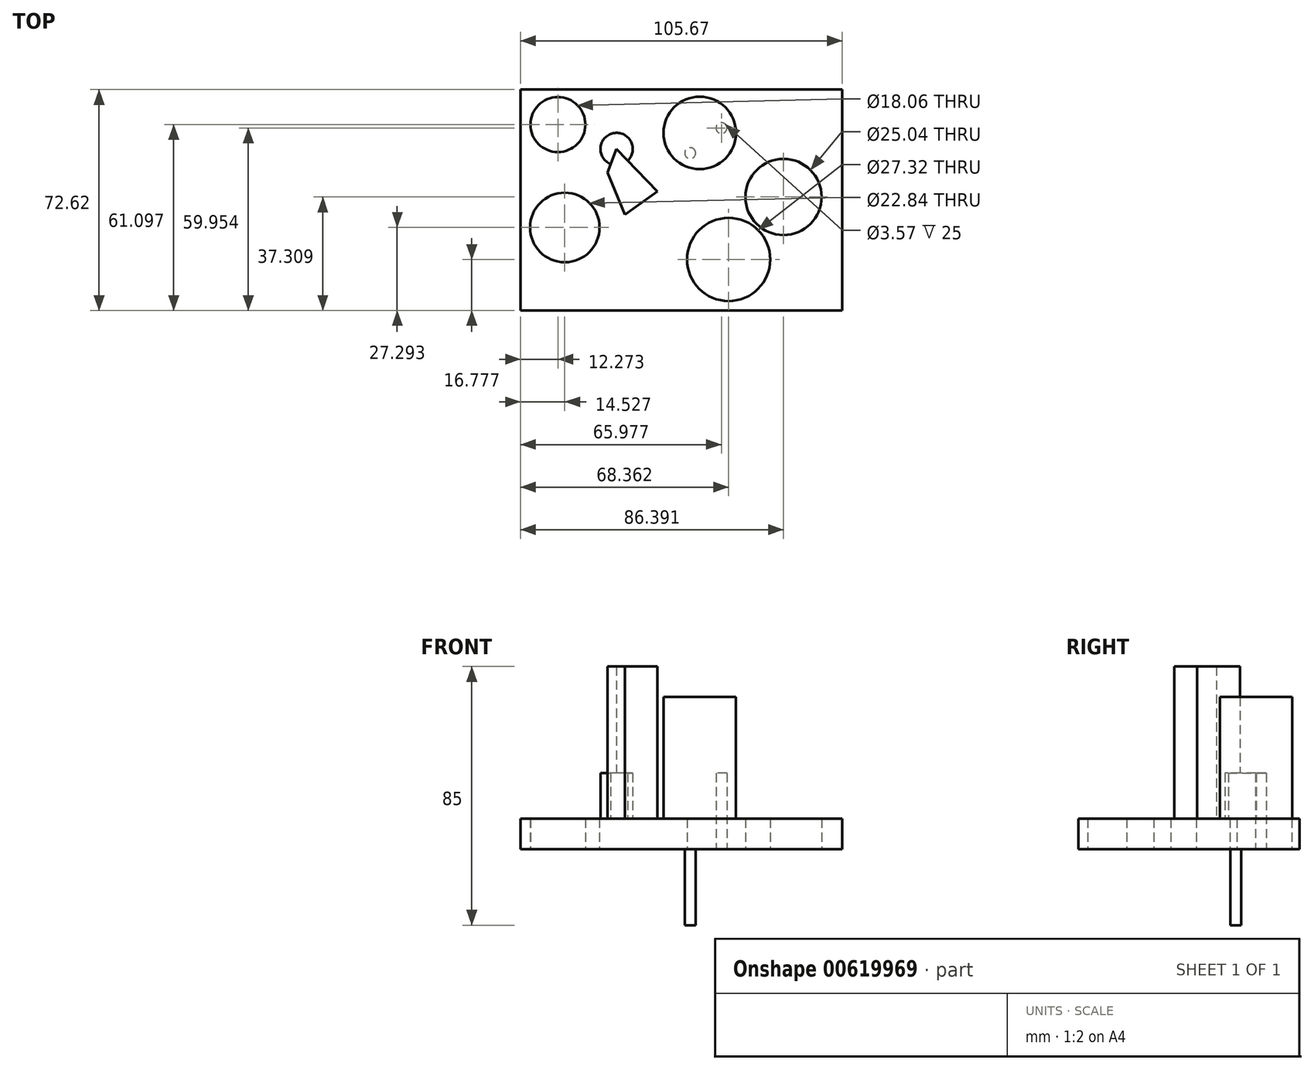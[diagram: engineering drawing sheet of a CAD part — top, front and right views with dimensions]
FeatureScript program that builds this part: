
annotation { "Feature Type Name" : "Feature", "Feature Type Description" : "" }
export const myFeature = defineFeature(function(context is Context, id is Id, definition is map)
    precondition{}
    {
        {
            var Q0;
            Q0=qCreatedBy(makeId("Top.planeOp"),FACE);
            var sketch = newSketch(context, id + "F0", { "sketchPlane" : qUnion([Q0])});
            skLineSegment(sketch, "E0.bottom", {"start": v(-44.95, 41.07) * mm, "end": v(60.72, 41.07) * mm});
            skLineSegment(sketch, "E0.top", {"start": v(-44.95, -31.55) * mm, "end": v(60.72, -31.55) * mm});
            skLineSegment(sketch, "E0.left", {"start": v(-44.95, 41.07) * mm, "end": v(-44.95, -31.55) * mm});
            skLineSegment(sketch, "E0.right", {"start": v(60.72, 41.07) * mm, "end": v(60.72, -31.55) * mm});
            skCircle(sketch, "E1", {"center": v(-32.68, 29.55) * mm, "radius": 9.03 * mm});
            skCircle(sketch, "E2", {"center": v(13.9, 26.8) * mm, "radius": 11.9 * mm});
            skCircle(sketch, "E3", {"center": v(41.44, 5.76) * mm, "radius": 12.52 * mm});
            skCircle(sketch, "E4", {"center": v(23.41, -14.77) * mm, "radius": 13.66 * mm});
            skCircle(sketch, "E5", {"center": v(-30.42, -4.26) * mm, "radius": 11.42 * mm});
            skLineSegment(sketch, "E6", {"start": v(-13.4, 21.53) * mm, "end": v(-16.4, 13.77) * mm});
            skLineSegment(sketch, "E7", {"start": v(-16.4, 13.77) * mm, "end": v(-10.72, 0) * mm});
            skLineSegment(sketch, "E8", {"start": v(-10.72, 0) * mm, "end": v(0, 7.51) * mm});
            skLineSegment(sketch, "E9", {"start": v(0, 7.51) * mm, "end": v(-13.4, 21.53) * mm});
            skArc(sketch, "E10", {"start": v(-9.73, 17.7) * mm, "mid": v(-14.43, 26.74) * mm, "end": v(-15.31, 16.58) * mm});
            skCircle(sketch, "E11", {"center": v(13.9, 26.8) * mm, "radius": 7.31 * mm, "construction": true});
            skCircle(sketch, "E12", {"center": v(6.6, 27.14) * mm, "radius": 1.78 * mm});
            skCircle(sketch, "E13", {"center": v(13.48, 34.1) * mm, "radius": 1.78 * mm});
            skCircle(sketch, "E14", {"center": v(21.03, 28.4) * mm, "radius": 1.78 * mm});
            skCircle(sketch, "E15", {"center": v(18.72, 21.3) * mm, "radius": 1.78 * mm});
            skCircle(sketch, "E16", {"center": v(10.77, 20.18) * mm, "radius": 1.78 * mm});
            skSolve(sketch);
        }
        {
            var Q0;
            Q0=makeQuery(id+"F0.imprint","IMPRINT",FACE,{"disambiguationData":[TD([[makeQuery(id+"F0.imprint","IMPRINT",EDGE,{"derivedFrom":sQuery(id+"F0.wireOp",EDGE,"E6")}),1.0]])]});
            extrude(context, id + "F1", {"entities" : qUnion([Q0]), "depth" : 60 * mm, "offsetDistance" : 25 * mm});
        }
        {
            var Q0;
            {var subQ3=sQuery(id+"F0.wireOp",EDGE,"E10");Q0=makeQuery(id+"F0.imprint","IMPRINT",FACE,{"disambiguationData":[TD([[makeQuery(id+"F0.imprint","IMPRINT",EDGE,{"derivedFrom":subQ3}),1.0]])]});}
            extrude(context, id + "F2", {"entities" : qUnion([Q0]), "operationType" : NewBodyOperationType.ADD, "depth" : 25 * mm, "offsetDistance" : 25 * mm});
        }
        {
            var Q0;
            Q0=makeQuery(id+"F0.imprint","IMPRINT",FACE,{"disambiguationData":[TD([[makeQuery(id+"F0.imprint","IMPRINT",EDGE,{"derivedFrom":sQuery(id+"F0.wireOp",EDGE,"E0.bottom")}),-1.0]])]});
            extrude(context, id + "F3", {"entities" : qUnion([Q0]), "operationType" : NewBodyOperationType.ADD, "depth" : 10 * mm, "offsetDistance" : 25 * mm});
        }
        {
            var Q0;
            Q0=makeQuery(id+"F0.imprint","IMPRINT",FACE,{"disambiguationData":[TD([[makeQuery(id+"F0.imprint","IMPRINT",EDGE,{"derivedFrom":sQuery(id+"F0.wireOp",EDGE,"E2")}),1.0]])]});
            var Q1;
            Q1=makeQuery(id+"F0.imprint","IMPRINT",FACE,{"disambiguationData":[TD([[makeQuery(id+"F0.imprint","IMPRINT",EDGE,{"derivedFrom":sQuery(id+"F0.wireOp",EDGE,"E13")}),1.0]])]});
            var Q2;
            Q2=makeQuery(id+"F0.imprint","IMPRINT",FACE,{"disambiguationData":[TD([[makeQuery(id+"F0.imprint","IMPRINT",EDGE,{"derivedFrom":sQuery(id+"F0.wireOp",EDGE,"E12")}),1.0]])]});
            var Q3;
            Q3=makeQuery(id+"F0.imprint","IMPRINT",FACE,{"disambiguationData":[TD([[makeQuery(id+"F0.imprint","IMPRINT",EDGE,{"derivedFrom":sQuery(id+"F0.wireOp",EDGE,"E16")}),1.0]])]});
            var Q4;
            Q4=makeQuery(id+"F0.imprint","IMPRINT",FACE,{"disambiguationData":[TD([[makeQuery(id+"F0.imprint","IMPRINT",EDGE,{"derivedFrom":sQuery(id+"F0.wireOp",EDGE,"E15")}),1.0]])]});
            var Q5;
            Q5=makeQuery(id+"F0.imprint","IMPRINT",FACE,{"disambiguationData":[TD([[makeQuery(id+"F0.imprint","IMPRINT",EDGE,{"derivedFrom":sQuery(id+"F0.wireOp",EDGE,"E14")}),1.0]])]});
            extrude(context, id + "F4", {"entities" : qUnion([Q0, Q1, Q2, Q3, Q4, Q5]), "operationType" : NewBodyOperationType.ADD, "depth" : 50 * mm, "offsetDistance" : 25 * mm});
        }
        {
            var Q0;
            Q0=makeQuery(id+"F0.imprint","IMPRINT",FACE,{"disambiguationData":[TD([[makeQuery(id+"F0.imprint","IMPRINT",EDGE,{"derivedFrom":sQuery(id+"F0.wireOp",EDGE,"E16")}),1.0]])]});
            var Q1;
            Q1=sQuery(id+"F0.wireOp",EDGE,"E12");
            var Q2;
            Q2=sQuery(id+"F0.wireOp",EDGE,"E16");
            var Q3;
            Q3=sQuery(id+"F0.wireOp",EDGE,"E15");
            var Q4;
            Q4=sQuery(id+"F0.wireOp",EDGE,"E14");
            var Q5;
            Q5=sQuery(id+"F0.wireOp",EDGE,"E13");
            extrude(context, id + "F5", {"entities" : qUnion([Q0]), "operationType" : NewBodyOperationType.ADD, "surfaceEntities" : qUnion([Q1, Q2, Q3, Q4, Q5]), "oppositeDirection" : true, "depth" : 25 * mm, "offsetDistance" : 25 * mm});
        }
        {
            var Q0;
            Q0=makeQuery(id+"F0.imprint","IMPRINT",FACE,{"disambiguationData":[TD([[makeQuery(id+"F0.imprint","IMPRINT",EDGE,{"derivedFrom":sQuery(id+"F0.wireOp",EDGE,"E14")}),1.0]])]});
            extrude(context, id + "F6", {"entities" : qUnion([Q0]), "operationType" : NewBodyOperationType.REMOVE, "depth" : 25 * mm, "offsetDistance" : 25 * mm});
        }
    });
